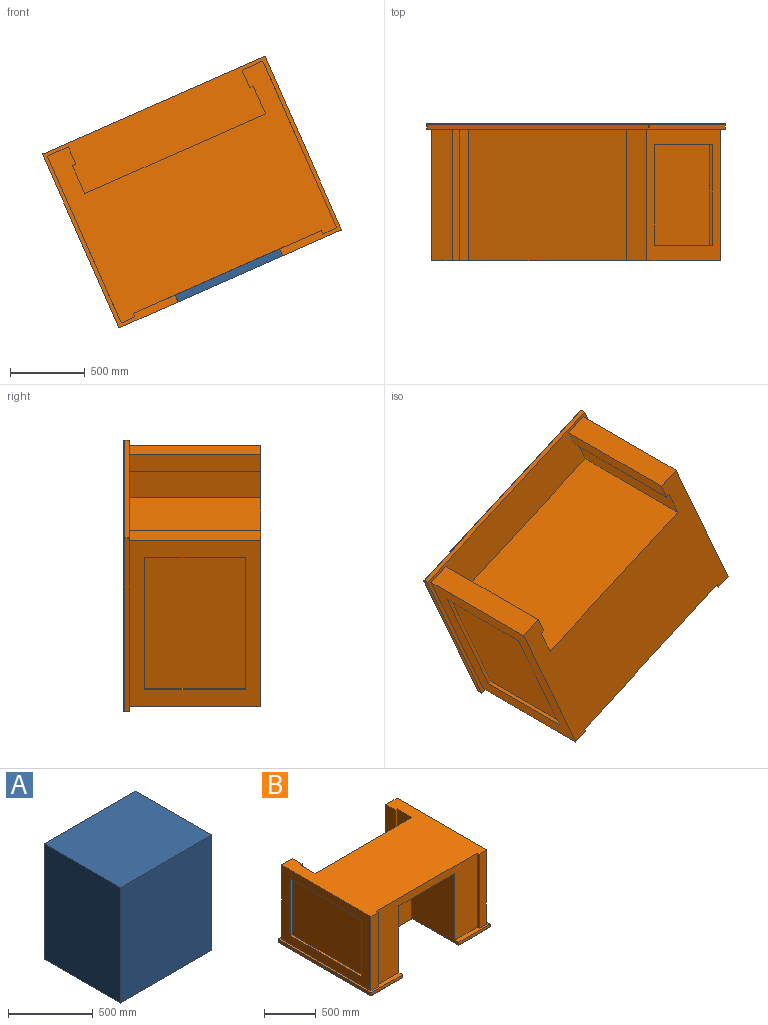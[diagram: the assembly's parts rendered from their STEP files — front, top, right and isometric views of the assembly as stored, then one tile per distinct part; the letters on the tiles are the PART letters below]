
ASSEMBLY  parts=2 mates=1
PART A: 6 faces, bbox 762x635x831.9 mm
  f0: plane 831.85x762mm, normal (0,-1,0), area 633869.7mm2, adj f1,f3,f4,f5
  f1: plane 831.85x635mm, normal (1,0,0), area 528224.8mm2, adj f0,f2,f4,f5
  f2: plane 831.85x762mm, normal (0,1,0), area 633869.7mm2, adj f1,f3,f4,f5
  f3: plane 831.85x635mm, normal (-1,0,0), area 528224.8mm2, adj f0,f2,f4,f5
  f4: plane 762x635mm, normal (0,0,1), area 483870mm2, adj f0,f1,f2,f3
  f5: plane 762x635mm, normal (0,0,-1), area 483870mm2, adj f0,f1,f2,f3
PART B: 58 faces, bbox 1625.6x1270x914.4 mm
  f0: plane 825.5x584.2mm, normal (1,0,0), area 482029.7mm2, adj f9,f23,f25,f33,f40,f57
  f1: plane 965.2x673.1mm, normal (1,0,0), area 649676.1mm2, adj f2,f3,f55,f56
  f2: plane 673.1x25.4mm, normal (0,-1,0), area 17096.7mm2, adj f1,f10,f55,f56
  f3: plane 673.1x25.4mm, normal (0,1,0), area 17096.7mm2, adj f1,f10,f55,f56
  f4: plane 965.2x673.1mm, normal (-1,0,0), area 649676.1mm2, adj f6,f7,f53,f54
  f5: plane 1625.6x1270mm, normal (0,0,1), area 570257.1mm2, adj f8,f10,f11,f12,f13,f14,f15,f16
  f6: plane 673.1x25.4mm, normal (0,-1,0), area 17096.7mm2, adj f4,f20,f53,f54
  f7: plane 673.1x25.4mm, normal (0,1,0), area 17096.7mm2, adj f4,f20,f53,f54
  f8: plane 421.64x33.02mm, normal (0,-1,0), area 13922.6mm2, adj f5,f35,f36,f50
  f9: plane 1615.44x1259.84mm, normal (0,0,-1), area 1551209.2mm2, adj f0,f23,f40,f42,f44,f46,f48,f50
  f10: plane 1219.2x876.3mm, normal (1,0,0), area 418708.8mm2, adj f2,f3,f5,f11,f27,f28,f55,f56
  f11: plane 876.3x152.4mm, normal (0,1,0), area 133548.1mm2, adj f5,f10,f12,f28
  f12: plane 876.3x127mm, normal (-1,0,0), area 111290.1mm2, adj f5,f11,f13,f28
  f13: plane 876.3x25.4mm, normal (0,-1,0), area 22258mm2, adj f5,f12,f14,f28
  f14: plane 876.3x203.2mm, normal (-1,0,0), area 178064.2mm2, adj f5,f13,f15,f28
  f15: plane 1320.8x876.3mm, normal (0,1,0), area 1157417mm2, adj f5,f14,f16,f28
  f16: plane 876.3x203.2mm, normal (1,0,0), area 178064.2mm2, adj f5,f15,f17,f28
  f17: plane 876.3x25.4mm, normal (0,-1,0), area 22258mm2, adj f5,f16,f18,f28
  f18: plane 876.3x127mm, normal (1,0,0), area 111290.1mm2, adj f5,f17,f19,f28
  f19: plane 876.3x152.4mm, normal (0,1,0), area 133548.1mm2, adj f5,f18,f20,f28
  f20: plane 1219.2x876.3mm, normal (-1,0,0), area 418708.8mm2, adj f5,f6,f7,f19,f21,f28,f53,f54
  f21: plane 876.3x101.6mm, normal (0,-1,0), area 89032.1mm2, adj f5,f20,f22,f28
  f22: plane 876.3x25.4mm, normal (1,0,0), area 22258mm2, adj f5,f21,f25,f28
  f23: plane 825.5x767.08mm, normal (0,-1,0), area 629036.5mm2, adj f0,f9,f24,f52,f57
  f24: plane 820.42x629.92mm, normal (-1,0,0), area 480799mm2, adj f5,f23,f25,f35,f52,f57
  f25: plane 1371.6x876.3mm, normal (0,-1,0), area 601934.3mm2, adj f0,f5,f22,f24,f26,f28,f57
  f26: plane 876.3x25.4mm, normal (-1,0,0), area 22258mm2, adj f5,f25,f27,f28
  f27: plane 876.3x101.6mm, normal (0,-1,0), area 89032.1mm2, adj f5,f10,f26,f28
  f28: plane 1574.8x1219.2mm, normal (0,0,1), area 1455481mm2, adj f10,f11,f12,f13,f14,f15,f16,f17
  f29: plane 420.52x33.02mm, normal (0,-1,0), area 13885.7mm2, adj f5,f34,f39,f42
  f30: plane 1259.84x33.02mm, normal (1,0,0), area 41599.9mm2, adj f5,f36,f37,f48
  f31: plane 1615.44x33.02mm, normal (0,1,0), area 53341.8mm2, adj f5,f37,f38,f46
  f32: plane 1259.84x33.02mm, normal (-1,0,0), area 41599.9mm2, adj f5,f38,f39,f44
  f33: plane 45.84x33.02mm, normal (1,-0.02,0), area 1514.2mm2, adj f0,f5,f34,f40
  f34: cylinder r=5.08mm len=33.02mm, axis (0,0,-1), area 259.4mm2, adj f5,f29,f33,f41
  f35: cylinder r=5.08mm len=33.02mm, axis (0,0,-1), area 263.5mm2, adj f5,f8,f24,f51
  f36: cylinder r=5.08mm len=33.02mm, axis (0,0,-1), area 263.5mm2, adj f5,f8,f30,f49
  f37: cylinder r=5.08mm len=33.02mm, axis (0,0,1), area 263.5mm2, adj f5,f30,f31,f47
  f38: cylinder r=5.08mm len=33.02mm, axis (0,0,-1), area 263.5mm2, adj f5,f31,f32,f45
  f39: cylinder r=5.08mm len=33.02mm, axis (0,0,1), area 263.5mm2, adj f5,f29,f32,f43
  f40: cylinder r=5.08mm len=254.42mm, axis (-0.02,-1,0), area 970.6mm2, adj f0,f9,f33,f41
  f41: sphere r=5.08mm, area 39.9mm2, adj f34,f40,f42
  f42: cylinder r=5.08mm len=420.52mm, axis (-1,0,0), area 3355.6mm2, adj f9,f29,f41,f43
  f43: sphere r=5.08mm, area 40.5mm2, adj f39,f42,f44
  f44: cylinder r=5.08mm len=1259.84mm, axis (0,1,0), area 10053.1mm2, adj f9,f32,f43,f45
  f45: sphere r=5.08mm, area 40.5mm2, adj f38,f44,f46
  f46: cylinder r=5.08mm len=1615.44mm, axis (1,0,0), area 12890.6mm2, adj f9,f31,f45,f47
  f47: sphere r=5.08mm, area 40.5mm2, adj f37,f46,f48
  f48: cylinder r=5.08mm len=1259.84mm, axis (0,-1,0), area 10053.1mm2, adj f9,f30,f47,f49
  f49: sphere r=5.08mm, area 40.5mm2, adj f36,f48,f50
  f50: cylinder r=5.08mm len=421.64mm, axis (-1,0,0), area 3364.5mm2, adj f8,f9,f49,f51
  f51: sphere r=5.08mm, area 40.5mm2, adj f35,f50,f52
  f52: cylinder r=5.08mm len=629.92mm, axis (0,1,0), area 5026.5mm2, adj f9,f23,f24,f51
  f53: plane 965.2x25.4mm, normal (0,0,1), area 24516.1mm2, adj f4,f6,f7,f20
  f54: plane 965.2x25.4mm, normal (0,0,-1), area 24516.1mm2, adj f4,f6,f7,f20
  f55: plane 965.2x25.4mm, normal (0,0,1), area 24516.1mm2, adj f1,f2,f3,f10
  f56: plane 965.2x25.4mm, normal (0,0,-1), area 24516.1mm2, adj f1,f2,f3,f10
  f57: plane 762x584.2mm, normal (0,0,-1), area 445160.4mm2, adj f0,f23,f24,f25
PLACE A rot(axis=(0.96,-0.2,0.2),92.4deg) t=(1381.5,989.94,-150.2)mm
PLACE B rot(axis=(0.96,-0.2,0.2),92.4deg) t=(1253.3,948.66,140.27)mm
MATE fastened A.f2 <-> B.f23  axis (-0.4,0,0.91) through (1253.31,574.01,140.27)mm
